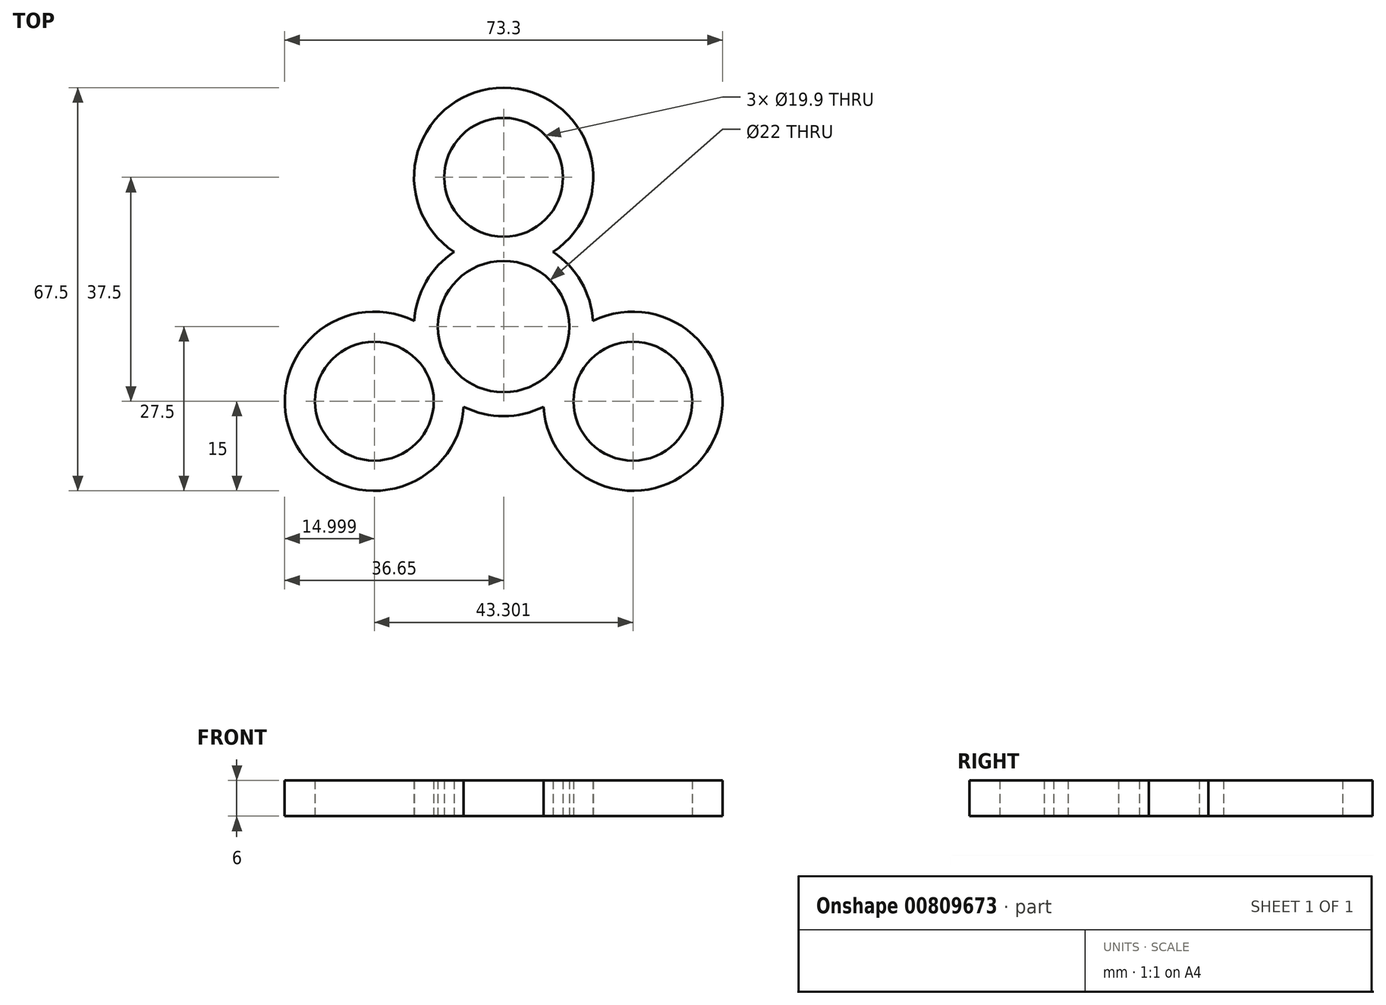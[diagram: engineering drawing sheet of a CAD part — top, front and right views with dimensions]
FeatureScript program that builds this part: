
annotation { "Feature Type Name" : "Feature", "Feature Type Description" : "" }
export const myFeature = defineFeature(function(context is Context, id is Id, definition is map)
    precondition{}
    {
        {
            var Q0;
            Q0=qCreatedBy(makeId("Top.planeOp"),FACE);
            var sketch = newSketch(context, id + "F0", { "sketchPlane" : qUnion([Q0])});
            skArc(sketch, "E0", {"start": v(9.53, 5.5) * mm, "mid": v(0, 11) * mm, "end": v(-9.53, 5.5) * mm});
            skCircle(sketch, "E1", {"center": v(0, 25) * mm, "radius": 9.95 * mm});
            skArc(sketch, "E2", {"start": v(13, 7.5) * mm, "mid": v(10.93, 10.27) * mm, "end": v(8.3, 12.5) * mm});
            skArc(sketch, "E3", {"start": v(8.3, 12.5) * mm, "mid": v(0, 40) * mm, "end": v(-8.3, 12.5) * mm});
            skArc(sketch, "E4.trimOffspring", {"start": v(-8.3, 12.5) * mm, "mid": v(-10.93, 10.27) * mm, "end": v(-13, 7.5) * mm});
            skCircle(sketch, "E5.1.0", {"center": v(-21.65, -12.5) * mm, "radius": 9.95 * mm});
            skArc(sketch, "E5.1.1", {"start": v(-13, 7.5) * mm, "mid": v(-14.36, 4.33) * mm, "end": v(-14.97, 0.93) * mm});
            skArc(sketch, "E5.1.2", {"start": v(-9.53, 5.5) * mm, "mid": v(-9.53, -5.5) * mm, "end": v(0, -11) * mm});
            skArc(sketch, "E5.1.3", {"start": v(-14.97, 0.93) * mm, "mid": v(-34.64, -20) * mm, "end": v(-6.68, -13.43) * mm});
            skArc(sketch, "E5.1.4", {"start": v(-6.68, -13.43) * mm, "mid": v(-3.43, -14.6) * mm, "end": v(0, -15) * mm});
            skCircle(sketch, "E5.2.0", {"center": v(21.65, -12.5) * mm, "radius": 9.95 * mm});
            skArc(sketch, "E5.2.1", {"start": v(0, -15) * mm, "mid": v(3.43, -14.6) * mm, "end": v(6.68, -13.43) * mm});
            skArc(sketch, "E5.2.2", {"start": v(0, -11) * mm, "mid": v(9.53, -5.5) * mm, "end": v(9.53, 5.5) * mm});
            skArc(sketch, "E5.2.3", {"start": v(6.68, -13.43) * mm, "mid": v(34.64, -20) * mm, "end": v(14.97, 0.93) * mm});
            skArc(sketch, "E5.2.4", {"start": v(14.97, 0.93) * mm, "mid": v(14.36, 4.33) * mm, "end": v(13, 7.5) * mm});
            skSolve(sketch);
        }
        {
            var Q0;
            Q0 = qSketchRegion(id + "F0", true);
            extrude(context, id + "F1", {"entities" : qUnion([Q0]), "depth" : 6 * mm, "offsetDistance" : 25 * mm});
        }
    });
